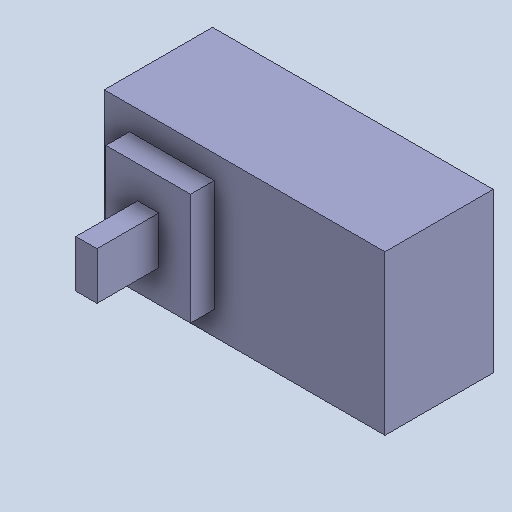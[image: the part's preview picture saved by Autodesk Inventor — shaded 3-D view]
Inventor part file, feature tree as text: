
AUTODESK INVENTOR PART (.ipt)
format: ipt  version: 2023 (Build 270158030, 158C)  size: 123,904 bytes
history: native  units: mm
features: extrude x3, sketch x3
ambient origin geometry x8: Origin, YZ Plane, XZ Plane, XY Plane, X Axis, Y Axis, Z Axis, Center Point
bodies: Body1 (feature_tree)
feature tree (6):
  extrude  "Extrusion6"  Depth=83.0mm
  extrude  "Extrusion7"  TaperAngle=0.0deg  [1 undecoded]
  extrude  "Extrusion8"  Depth=25.0mm
  sketch  "Sketch8"  dims[d31=47.0mm d32=83.0mm]
  sketch  "Sketch9"  dims[d33=32.0mm d34=0.0mm]
  sketch  "Sketch10"  dims[d35=20.0mm d36=25.0mm d37=33.0mm d38=7.0mm d39=0.0mm d40=20.0mm d41=14.0mm d42=6.25mm d43=18.28mm d44=0.0mm]
note: 1 required parameter value undecoded (feature->parameter linkage not recoverable at this tier; creation-order binding heuristic only, values carry confidence <= 0.55)
